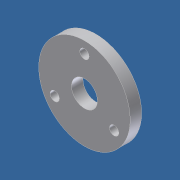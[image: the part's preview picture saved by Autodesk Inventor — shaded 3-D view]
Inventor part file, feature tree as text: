
AUTODESK INVENTOR PART (.ipt)
format: ipt  version: unknown  size: 177,664 bytes
history: native  units: in
note: dims shown in document units (in); Inventor stores cm internally (conversion verified against a paired STEP export)
features: sketch x2, extrude x1, hole x1
ambient origin geometry x8: Origin, YZ Plane, XZ Plane, XY Plane, X Axis, Y Axis, Z Axis, Center Point
bodies: Solid1 (feature_tree)
feature tree (4):
  extrude  "Extrusion1"  Depth=0.567in
  hole  "Hole1"  [1 undecoded]
  sketch  "Sketch1"  dims[d0=2.0in d1=0.567in]
  sketch  "Sketch2"  dims[d2=0.25in d3=0.0in d7=0.203in d8=0.75in d9=0.375in d10=0.25in d11=0.5635in d12=1.0in d13=0.8108in]
note: 1 required parameter value undecoded (feature->parameter linkage not recoverable at this tier; creation-order binding heuristic only, values carry confidence <= 0.55)
